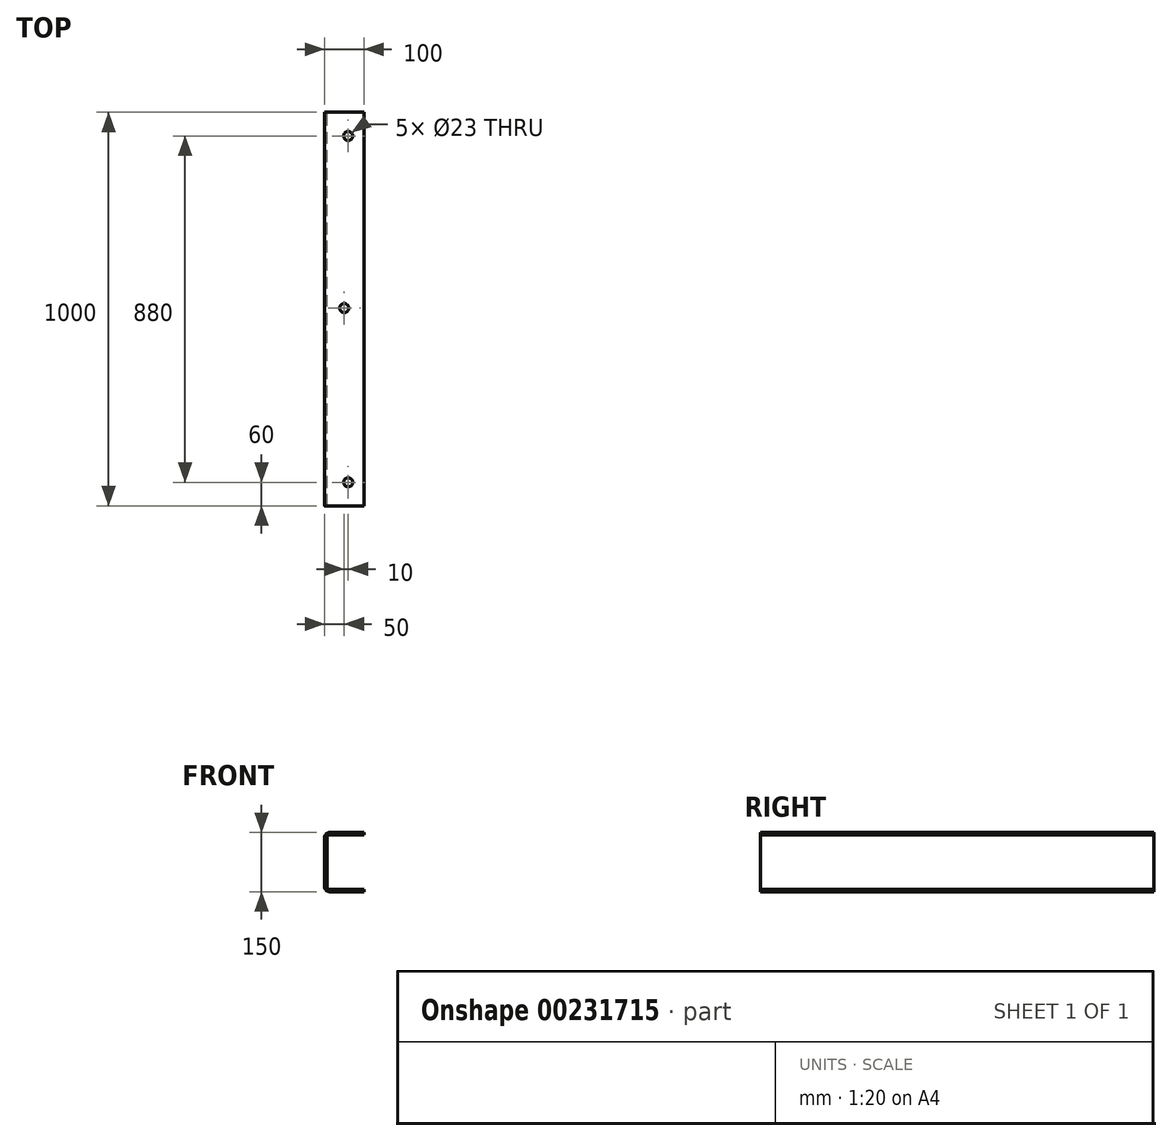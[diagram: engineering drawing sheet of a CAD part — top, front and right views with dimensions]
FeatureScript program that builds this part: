
annotation { "Feature Type Name" : "Feature", "Feature Type Description" : "" }
export const myFeature = defineFeature(function(context is Context, id is Id, definition is map)
    precondition{}
    {
        {
            var Q0;
            Q0=qCreatedBy(makeId("Front.planeOp"),FACE);
            var sketch = newSketch(context, id + "F0", { "sketchPlane" : qUnion([Q0])});
            skLineSegment(sketch, "E0.bottom", {"start": v(-38, 75) * mm, "end": v(50, 75) * mm});
            skLineSegment(sketch, "E0.top", {"start": v(-38, -75) * mm, "end": v(50, -75) * mm});
            skLineSegment(sketch, "E0.left", {"start": v(-50, 63) * mm, "end": v(-50, -63) * mm});
            skLineSegment(sketch, "E0.right", {"start": v(50, 75) * mm, "end": v(50, 69) * mm});
            skLineSegment(sketch, "E1.0", {"start": v(-44, 64) * mm, "end": v(-44, -64) * mm});
            skLineSegment(sketch, "E1.1", {"start": v(-39, 69) * mm, "end": v(50, 69) * mm});
            skLineSegment(sketch, "E2.0", {"start": v(-39, -69) * mm, "end": v(50, -69) * mm});
            skLineSegment(sketch, "E3.trimOffspring", {"start": v(50, -69) * mm, "end": v(50, -75) * mm});
            skPoint(sketch, "E4.visualSharp", {"position": v(-44, 69) * mm});
            skArc(sketch, "E4.filletArc", {"start": v(-39, 69) * mm, "mid": v(-42.54, 67.54) * mm, "end": v(-44, 64) * mm});
            skPoint(sketch, "E5.visualSharp", {"position": v(-44, -69) * mm});
            skArc(sketch, "E5.filletArc", {"start": v(-44, -64) * mm, "mid": v(-42.54, -67.54) * mm, "end": v(-39, -69) * mm});
            skPoint(sketch, "E6.visualSharp", {"position": v(-50, 75) * mm});
            skArc(sketch, "E6.filletArc", {"start": v(-38, 75) * mm, "mid": v(-46.49, 71.49) * mm, "end": v(-50, 63) * mm});
            skPoint(sketch, "E7.visualSharp", {"position": v(-50, -75) * mm});
            skArc(sketch, "E7.filletArc", {"start": v(-50, -63) * mm, "mid": v(-46.49, -71.49) * mm, "end": v(-38, -75) * mm});
            skSolve(sketch);
        }
        {
            var Q0;
            Q0=makeQuery(id+"F0.imprint","IMPRINT",FACE,{"disambiguationData":[TD([[makeQuery(id+"F0.imprint","IMPRINT",EDGE,{"derivedFrom":sQuery(id+"F0.wireOp",EDGE,"E0.bottom")}),-1.0]])]});
            extrude(context, id + "F1", {"entities" : qUnion([Q0]), "depth" : 1000 * mm});
        }
        {
            var Q0;
            Q0=makeQuery(id+"F1.opExtrude","SWEPT_FACE",FACE,{"disambiguationData":[OSD([sQuery(id+"F0.wireOp",EDGE,"E0.bottom")])]});
            var sketch = newSketch(context, id + "F2", { "sketchPlane" : qUnion([Q0])});
            skCircle(sketch, "E8", {"center": v(10, -60) * mm, "radius": 11.5 * mm});
            skCircle(sketch, "E9", {"center": v(10, -940) * mm, "radius": 11.5 * mm});
            skSolve(sketch);
        }
        {
            var Q0;
            Q0=makeQuery(id+"F2.imprint","IMPRINT",FACE,{"disambiguationData":[TD([[makeQuery(id+"F2.imprint","IMPRINT",EDGE,{"derivedFrom":sQuery(id+"F2.wireOp",EDGE,"E8")}),1.0]])]});
            var Q1;
            Q1=makeQuery(id+"F2.imprint","IMPRINT",FACE,{"disambiguationData":[TD([[makeQuery(id+"F2.imprint","IMPRINT",EDGE,{"derivedFrom":sQuery(id+"F2.wireOp",EDGE,"E9")}),1.0]])]});
            extrude(context, id + "F3", {"entities" : qUnion([Q0, Q1]), "operationType" : NewBodyOperationType.REMOVE, "oppositeDirection" : true, "depth" : 175 * mm});
        }
        {
            var Q0;
            Q0=makeQuery(id+"F1.opExtrude","SWEPT_BODY",BODY,{"disambiguationData":[OSD([sQuery(id+"F0.wireOp",EDGE,"E0.bottom"),sQuery(id+"F0.wireOp",EDGE,"E0.top"),sQuery(id+"F0.wireOp",EDGE,"E0.left"),sQuery(id+"F0.wireOp",EDGE,"E0.right"),sQuery(id+"F0.wireOp",EDGE,"E1.0"),sQuery(id+"F0.wireOp",EDGE,"E1.1"),sQuery(id+"F0.wireOp",EDGE,"E2.0"),sQuery(id+"F0.wireOp",EDGE,"E3.trimOffspring"),sQuery(id+"F0.wireOp",EDGE,"E4.filletArc"),sQuery(id+"F0.wireOp",EDGE,"E5.filletArc"),sQuery(id+"F0.wireOp",EDGE,"E6.filletArc"),sQuery(id+"F0.wireOp",EDGE,"E7.filletArc")])]});
            transform(context, id + "F4", {"entities" : qUnion([Q0]), "transformType" : TransformType.TRANSLATION_3D, "dx" : 300 * mm, "dy" : 0 * mm, "dz" : 0 * mm, "makeCopy" : true});
        }
        {
            var Q0;
            Q0=makeQuery(id+"F4.opPattern","COPY",BODY,{"derivedFrom":makeQuery(id+"F1.opExtrude","SWEPT_BODY",BODY,{"disambiguationData":[OSD([sQuery(id+"F0.wireOp",EDGE,"E0.bottom"),sQuery(id+"F0.wireOp",EDGE,"E0.top"),sQuery(id+"F0.wireOp",EDGE,"E0.left"),sQuery(id+"F0.wireOp",EDGE,"E0.right"),sQuery(id+"F0.wireOp",EDGE,"E1.0"),sQuery(id+"F0.wireOp",EDGE,"E1.1"),sQuery(id+"F0.wireOp",EDGE,"E2.0"),sQuery(id+"F0.wireOp",EDGE,"E3.trimOffspring"),sQuery(id+"F0.wireOp",EDGE,"E4.filletArc"),sQuery(id+"F0.wireOp",EDGE,"E5.filletArc"),sQuery(id+"F0.wireOp",EDGE,"E6.filletArc"),sQuery(id+"F0.wireOp",EDGE,"E7.filletArc")])]}),"instanceName":"1"});
            deleteBodies(context, id + "F5", {"entities" : qUnion([Q0])});
        }
        {
            var Q0;
            Q0=makeQuery(id+"F1.opExtrude","SWEPT_FACE",FACE,{"disambiguationData":[OSD([sQuery(id+"F0.wireOp",EDGE,"E0.bottom")])]});
            var sketch = newSketch(context, id + "F6", { "sketchPlane" : qUnion([Q0])});
            skCircle(sketch, "E10", {"center": v(0, -497.36) * mm, "radius": 11.5 * mm});
            skSolve(sketch);
        }
        {
            var Q0;
            Q0=makeQuery(id+"F6.imprint","IMPRINT",FACE,{"disambiguationData":[TD([[makeQuery(id+"F6.imprint","IMPRINT",EDGE,{"derivedFrom":sQuery(id+"F6.wireOp",EDGE,"E10")}),1.0]])]});
            extrude(context, id + "F7", {"entities" : qUnion([Q0]), "operationType" : NewBodyOperationType.REMOVE, "oppositeDirection" : true, "depth" : 25 * mm});
        }
    });
